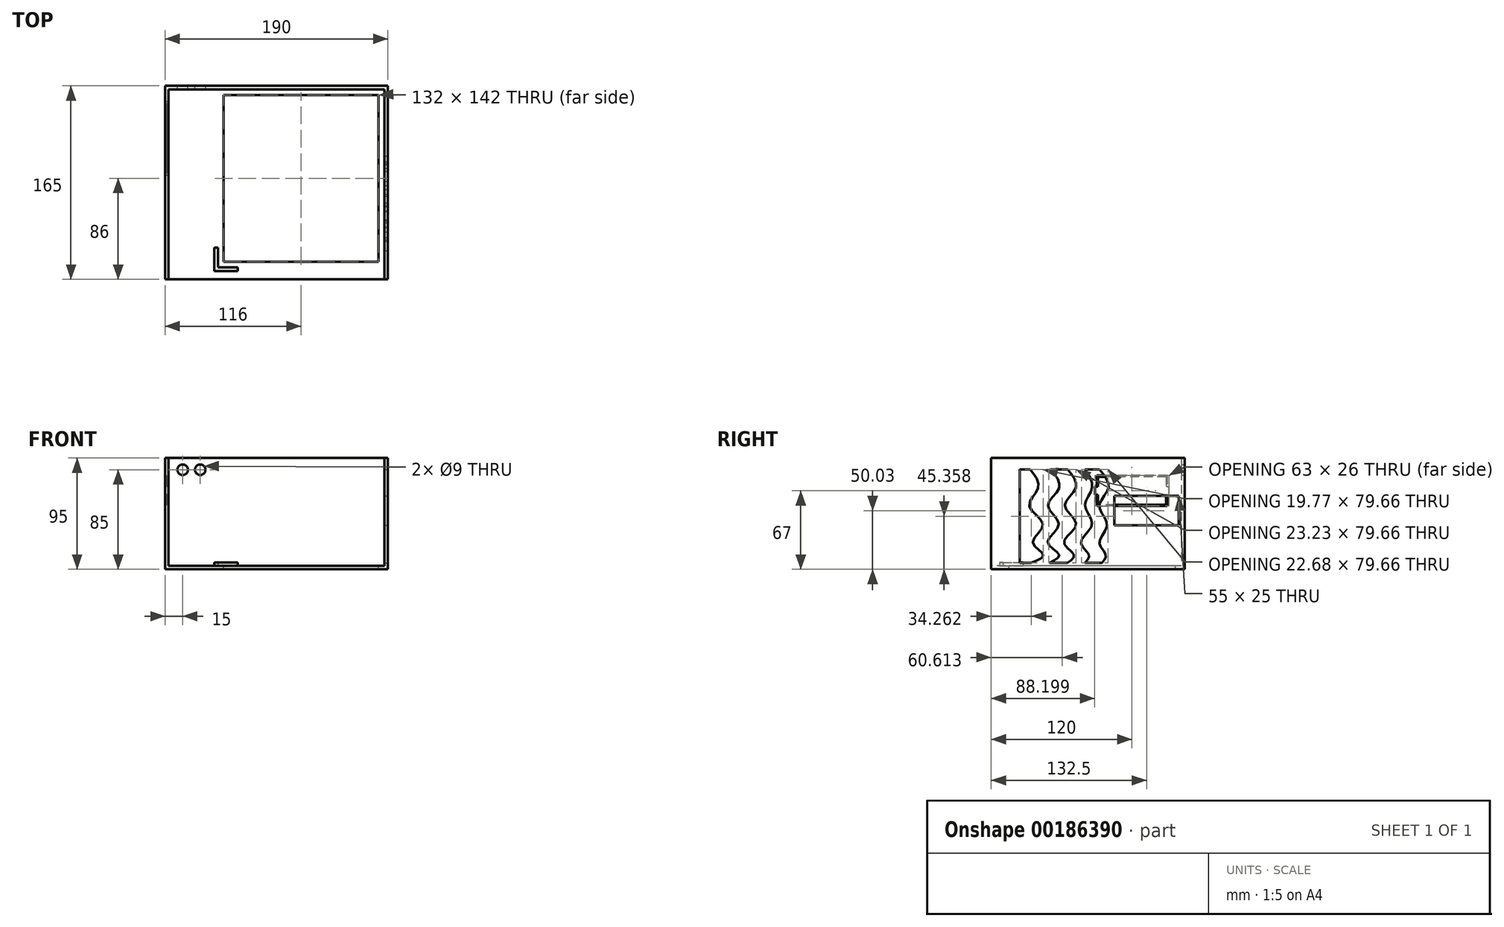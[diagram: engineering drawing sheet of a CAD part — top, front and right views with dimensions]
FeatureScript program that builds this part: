
annotation { "Feature Type Name" : "Feature", "Feature Type Description" : "" }
export const myFeature = defineFeature(function(context is Context, id is Id, definition is map)
    precondition{}
    {
        {
            var Q0;
            Q0=qCreatedBy(makeId("Top.planeOp"),FACE);
            var sketch = newSketch(context, id + "F0", { "sketchPlane" : qUnion([Q0])});
            skLineSegment(sketch, "E0.bottom", {"start": v(-95, 85) * mm, "end": v(95, 85) * mm});
            skLineSegment(sketch, "E0.top", {"start": v(-95, -85) * mm, "end": v(95, -85) * mm});
            skLineSegment(sketch, "E0.left", {"start": v(-95, 85) * mm, "end": v(-95, -85) * mm});
            skLineSegment(sketch, "E0.right", {"start": v(95, 85) * mm, "end": v(95, -85) * mm});
            skPoint(sketch, "E0.middle", {"position": v(0, 0) * mm});
            skSolve(sketch);
        }
        {
            var Q0;
            Q0=makeQuery(id+"F0.imprint","IMPRINT",FACE,{"disambiguationData":[TD([[makeQuery(id+"F0.imprint","IMPRINT",EDGE,{"derivedFrom":sQuery(id+"F0.wireOp",EDGE,"E0.bottom")}),-1.0]])]});
            extrude(context, id + "F1", {"entities" : qUnion([Q0]), "depth" : 95 * mm});
        }
        {
            var Q0;
            Q0=makeQuery(id+"F1.opExtrude","CAP_FACE",FACE,{"disambiguationData":[OSD([sQuery(id+"F0.wireOp",EDGE,"E0.bottom"),sQuery(id+"F0.wireOp",EDGE,"E0.top"),sQuery(id+"F0.wireOp",EDGE,"E0.left"),sQuery(id+"F0.wireOp",EDGE,"E0.right")])],"isStart":false});
            var Q1;
            Q1=makeQuery(id+"F1.opExtrude","SWEPT_FACE",FACE,{"disambiguationData":[OSD([sQuery(id+"F0.wireOp",EDGE,"E0.top")])]});
            shell(context, id + "F2", {"entities" : qUnion([Q0, Q1]), "thickness" : 3 * mm});
        }
        {
            var Q0;
            Q0=makeQuery(id+"F2.opShell","OFFSET_FACE",FACE,{"disambiguationData":[OSD([sQuery(id+"F0.wireOp",EDGE,"E0.bottom"),sQuery(id+"F0.wireOp",EDGE,"E0.top"),sQuery(id+"F0.wireOp",EDGE,"E0.left"),sQuery(id+"F0.wireOp",EDGE,"E0.right")])]});
            var sketch = newSketch(context, id + "F3", { "sketchPlane" : qUnion([Q0])});
            skLineSegment(sketch, "E1.bottom", {"start": v(92, 82) * mm, "end": v(-50, 82) * mm});
            skLineSegment(sketch, "E1.top", {"start": v(92, -70) * mm, "end": v(-50, -70) * mm, "construction": true});
            skLineSegment(sketch, "E1.left", {"start": v(92, 82) * mm, "end": v(92, -70) * mm});
            skLineSegment(sketch, "E1.right", {"start": v(-50, 82) * mm, "end": v(-50, -70) * mm, "construction": true});
            skLineSegment(sketch, "E2.top", {"start": v(-50, -53) * mm, "end": v(-53, -53) * mm});
            skLineSegment(sketch, "E2.left", {"start": v(-50, -70) * mm, "end": v(-50, -53) * mm});
            skLineSegment(sketch, "E2.right", {"start": v(-53, -70) * mm, "end": v(-53, -53) * mm});
            skLineSegment(sketch, "E3.bottom", {"start": v(-50, -70) * mm, "end": v(-33, -70) * mm});
            skLineSegment(sketch, "E3.top", {"start": v(-53, -73) * mm, "end": v(-33, -73) * mm});
            skLineSegment(sketch, "E3.left", {"start": v(-53, -70) * mm, "end": v(-53, -73) * mm});
            skLineSegment(sketch, "E3.right", {"start": v(-33, -70) * mm, "end": v(-33, -73) * mm});
            skSolve(sketch);
        }
        {
            var Q0;
            Q0=makeQuery(id+"F3.imprint","IMPRINT",FACE,{"disambiguationData":[TD([[makeQuery(id+"F3.imprint","IMPRINT",EDGE,{"derivedFrom":sQuery(id+"F3.wireOp",EDGE,"E2.top")}),1.0]])]});
            extrude(context, id + "F4", {"entities" : qUnion([Q0]), "operationType" : NewBodyOperationType.ADD, "depth" : 3 * mm});
        }
        {
            var Q0;
            Q0=makeQuery(id+"F1.opExtrude","SWEPT_FACE",FACE,{"disambiguationData":[OSD([sQuery(id+"F0.wireOp",EDGE,"E0.right")])]});
            var sketch = newSketch(context, id + "F5", { "sketchPlane" : qUnion([Q0])});
            skLineSegment(sketch, "E4.bottom", {"start": v(85, 95) * mm, "end": v(-67, 95) * mm});
            skLineSegment(sketch, "E4.top", {"start": v(85, 3) * mm, "end": v(-67, 3) * mm});
            skLineSegment(sketch, "E4.left", {"start": v(85, 95) * mm, "end": v(85, 3) * mm});
            skLineSegment(sketch, "E4.right", {"start": v(-67, 95) * mm, "end": v(-67, 3) * mm});
            skLineSegment(sketch, "E5.0", {"start": v(-22, 85.19) * mm, "end": v(29.77, 85.19) * mm});
            skLineSegment(sketch, "E6.bottom", {"start": v(-55.62, 85.19) * mm, "end": v(80, 85.19) * mm});
            skLineSegment(sketch, "E6.top", {"start": v(-55.62, 5.53) * mm, "end": v(80, 5.53) * mm});
            skLineSegment(sketch, "E6.left", {"start": v(-55.62, 85.19) * mm, "end": v(-55.62, 5.53) * mm});
            skLineSegment(sketch, "E6.right", {"start": v(80, 85.19) * mm, "end": v(80, 5.53) * mm});
            skLineSegment(sketch, "E7.bottom", {"start": v(80, 37.53) * mm, "end": v(25, 37.53) * mm});
            skLineSegment(sketch, "E7.top", {"start": v(80, 62.53) * mm, "end": v(25, 62.53) * mm});
            skLineSegment(sketch, "E7.left", {"start": v(80, 37.53) * mm, "end": v(80, 62.53) * mm});
            skLineSegment(sketch, "E7.right", {"start": v(25, 37.53) * mm, "end": v(25, 62.53) * mm});
            skPoint(sketch, "E8.orphan", {"position": v(3.89, 5.53) * mm});
            skFitSpline(sketch, "E9", {"points": [v(-46.65, 85.19) * mm, v(-39.93, 69.5) * mm, v(-47.64, 54.07) * mm, v(-35.97, 38.25) * mm, v(-44.47, 23.03) * mm, v(-35.78, 12.55) * mm, v(-46.25, 5.53) * mm], "startDerivative": vector(72.14, -91.85) * mm, "endDerivative": vector(-114.34, -43.57) * mm});
            skFitSpline(sketch, "E10", {"points": [v(-29.25, 85.19) * mm, v(-22.13, 69.5) * mm, v(-31.62, 54.07) * mm, v(-22.33, 38.25) * mm, v(-31.82, 23.03) * mm, v(-22.13, 12.55) * mm, v(-30.24, 5.53) * mm], "startDerivative": vector(76.45, -91.72) * mm, "endDerivative": vector(-99.1, -48.82) * mm});
            skFitSpline(sketch, "E11", {"points": [v(-14.82, 85.19) * mm, v(-7.9, 69.5) * mm, v(-17.19, 54.07) * mm, v(-7.7, 38.25) * mm, v(-17.98, 23.03) * mm, v(-9.48, 12.55) * mm, v(-15.01, 5.53) * mm], "startDerivative": vector(73.81, -90.58) * mm, "endDerivative": vector(-76.43, -53.52) * mm});
            skFitSpline(sketch, "E12", {"points": [v(0, 85.19) * mm, v(5.94, 69.5) * mm, v(0, 54.07) * mm, v(5.94, 38.25) * mm, v(-3.55, 23.03) * mm, v(3.18, 12.55) * mm, v(0, 5.53) * mm], "startDerivative": vector(57.94, -87.76) * mm, "endDerivative": vector(-49.7, -56.04) * mm});
            skPoint(sketch, "E13.2.internal.snap0", {"position": v(12.19, 85.19) * mm});
            skPoint(sketch, "E13.4.internal.snap0", {"position": v(12.19, 85.19) * mm});
            skFitSpline(sketch, "E13", {"points": [v(12.19, 85.19) * mm, v(19.98, 69.5) * mm, v(12.19, 54.07) * mm, v(18.8, 38.25) * mm, v(12.19, 23.03) * mm, v(17.6, 12.55) * mm, v(14.45, 5.53) * mm], "startDerivative": vector(72.92, -85.74) * mm, "endDerivative": vector(-46.67, -55.62) * mm});
            skSolve(sketch);
        }
        {
            var Q0;
            Q0=makeQuery(id+"F1.opExtrude","SWEPT_FACE",FACE,{"disambiguationData":[OSD([sQuery(id+"F0.wireOp",EDGE,"E0.left")])]});
            var sketch = newSketch(context, id + "F6", { "sketchPlane" : qUnion([Q0])});
            skLineSegment(sketch, "E14.bottom", {"start": v(85, 95) * mm, "end": v(80, 95) * mm});
            skLineSegment(sketch, "E14.top", {"start": v(85, 0) * mm, "end": v(80, 0) * mm});
            skLineSegment(sketch, "E14.left", {"start": v(85, 95) * mm, "end": v(85, 0) * mm});
            skLineSegment(sketch, "E14.right", {"start": v(80, 95) * mm, "end": v(80, 0) * mm});
            skSolve(sketch);
        }
        {
            var Q0;
            Q0=makeQuery(id+"F6.imprint","IMPRINT",FACE,{"disambiguationData":[TD([[makeQuery(id+"F6.imprint","IMPRINT",EDGE,{"derivedFrom":sQuery(id+"F6.wireOp",EDGE,"E14.bottom")}),-1.0]])]});
            var Q1;
            Q1=makeQuery(id+"F1.opExtrude","SWEPT_FACE",FACE,{"disambiguationData":[OSD([sQuery(id+"F0.wireOp",EDGE,"E0.right")])]});
            extrude(context, id + "F7", {"entities" : qUnion([Q0]), "operationType" : NewBodyOperationType.REMOVE, "endBound" : BoundingType.UP_TO_SURFACE, "oppositeDirection" : true, "endBoundEntityFace" : qUnion([Q1]), "depth" : 25 * mm});
        }
        {
            var Q0;
            Q0=makeQuery(id+"F5.imprint","IMPRINT",FACE,{"disambiguationData":[TD([[makeQuery(id+"F5.imprint","IMPRINT",EDGE,{"derivedFrom":sQuery(id+"F5.wireOp",EDGE,"E7.bottom")}),-1.0]])]});
            var Q1;
            {var subQ0=sQuery(id+"F5.wireOp",EDGE,"E12");Q1=makeQuery(id+"F5.imprint","IMPRINT",FACE,{"disambiguationData":[TD([[makeQuery(id+"F5.imprint","IMPRINT",EDGE,{"derivedFrom":subQ0}),1.0]])]});}
            var Q2;
            {var subQ3=sQuery(id+"F5.wireOp",EDGE,"E10");Q2=makeQuery(id+"F5.imprint","IMPRINT",FACE,{"disambiguationData":[TD([[makeQuery(id+"F5.imprint","IMPRINT",EDGE,{"derivedFrom":subQ3}),1.0]])]});}
            var Q3;
            {var subQ0=sQuery(id+"F5.wireOp",EDGE,"E6.left");Q3=makeQuery(id+"F5.imprint","IMPRINT",FACE,{"disambiguationData":[TD([[makeQuery(id+"F5.imprint","IMPRINT",EDGE,{"derivedFrom":subQ0}),1.0]])]});}
            extrude(context, id + "F8", {"entities" : qUnion([Q0, Q1, Q2, Q3]), "operationType" : NewBodyOperationType.REMOVE, "oppositeDirection" : true, "depth" : 25 * mm});
        }
        {
            var Q0;
            Q0=makeQuery(id+"F1.opExtrude","SWEPT_FACE",FACE,{"disambiguationData":[OSD([sQuery(id+"F0.wireOp",EDGE,"E0.bottom")])]});
            var sketch = newSketch(context, id + "F9", { "sketchPlane" : qUnion([Q0])});
            skPoint(sketch, "E15", {"position": v(65, 85) * mm});
            skPoint(sketch, "E16", {"position": v(80, 85) * mm});
            skSolve(sketch);
        }
        {
            var Q0;
            Q0=sQuery(id+"F9.wireOp",VERTEX,"E15");
            var Q1;
            Q1=sQuery(id+"F9.wireOp",VERTEX,"E16");
            var Q2;
            Q2=makeQuery(id+"F1.opExtrude","SWEPT_BODY",BODY,{"disambiguationData":[OSD([sQuery(id+"F0.wireOp",EDGE,"E0.bottom"),sQuery(id+"F0.wireOp",EDGE,"E0.top"),sQuery(id+"F0.wireOp",EDGE,"E0.left"),sQuery(id+"F0.wireOp",EDGE,"E0.right")])]});
            hole(context, id + "F10", {"style" : HoleStyle.SIMPLE, "endStyle" : HoleEndStyle.THROUGH, "holeDiameter" : 9 * mm, "locations" : qUnion([Q0, Q1]), "scope" : qUnion([Q2]), "isTappedThrough" : true});
        }
        {
            var Q0;
            Q0=makeQuery(id+"F1.opExtrude","SWEPT_FACE",FACE,{"disambiguationData":[OSD([sQuery(id+"F0.wireOp",EDGE,"E0.left")])]});
            var sketch = newSketch(context, id + "F11", { "sketchPlane" : qUnion([Q0])});
            skLineSegment(sketch, "E17.bottom", {"start": v(-70, 80) * mm, "end": v(-10, 80) * mm});
            skLineSegment(sketch, "E17.top", {"start": v(-70, 54) * mm, "end": v(-10, 54) * mm});
            skLineSegment(sketch, "E17.left", {"start": v(-70, 80) * mm, "end": v(-70, 54) * mm});
            skLineSegment(sketch, "E17.right", {"start": v(-10, 80) * mm, "end": v(-10, 54) * mm});
            skLineSegment(sketch, "E18.bottom", {"start": v(-69, 79) * mm, "end": v(-11, 79) * mm});
            skLineSegment(sketch, "E18.top", {"start": v(-69, 55) * mm, "end": v(-11, 55) * mm});
            skLineSegment(sketch, "E18.left", {"start": v(-69, 79) * mm, "end": v(-69, 55) * mm});
            skLineSegment(sketch, "E18.right", {"start": v(-11, 79) * mm, "end": v(-11, 55) * mm});
            skSolve(sketch);
        }
        {
            var Q0;
            Q0=makeQuery(id+"F11.imprint","IMPRINT",FACE,{"disambiguationData":[TD([[makeQuery(id+"F11.imprint","IMPRINT",EDGE,{"derivedFrom":sQuery(id+"F11.wireOp",EDGE,"E18.bottom")}),-1.0]])]});
            extrude(context, id + "F12", {"entities" : qUnion([Q0]), "operationType" : NewBodyOperationType.REMOVE, "endBound" : BoundingType.UP_TO_NEXT, "oppositeDirection" : true, "depth" : 25 * mm});
        }
        {
            var Q0;
            Q0=makeQuery(id+"F11.imprint","IMPRINT",FACE,{"disambiguationData":[TD([[makeQuery(id+"F11.imprint","IMPRINT",EDGE,{"derivedFrom":sQuery(id+"F11.wireOp",EDGE,"E17.bottom")}),-1.0]])]});
            extrude(context, id + "F13", {"entities" : qUnion([Q0]), "operationType" : NewBodyOperationType.REMOVE, "oppositeDirection" : true, "depth" : 1 * mm});
        }
        {
            var Q0;
            Q0=makeQuery(id+"F2.opShell","OFFSET_FACE",FACE,{"disambiguationData":[OSD([sQuery(id+"F0.wireOp",EDGE,"E0.left")])]});
            var sketch = newSketch(context, id + "F14", { "sketchPlane" : qUnion([Q0])});
            skLineSegment(sketch, "E19.bottom", {"start": v(10, 80) * mm, "end": v(70, 80) * mm});
            skLineSegment(sketch, "E19.top", {"start": v(10, 54) * mm, "end": v(70, 54) * mm});
            skLineSegment(sketch, "E19.left", {"start": v(10, 80) * mm, "end": v(10, 54) * mm});
            skLineSegment(sketch, "E19.right", {"start": v(70, 80) * mm, "end": v(70, 54) * mm});
            skSolve(sketch);
        }
        {
            var Q0;
            Q0=makeQuery(id+"F14.imprint","IMPRINT",FACE,{"disambiguationData":[TD([[makeQuery(id+"F14.imprint","IMPRINT",EDGE,{"derivedFrom":sQuery(id+"F14.wireOp",EDGE,"E19.bottom")}),-1.0]])]});
            extrude(context, id + "F15", {"entities" : qUnion([Q0]), "operationType" : NewBodyOperationType.REMOVE, "oppositeDirection" : true, "depth" : 1 * mm});
        }
        {
            var Q0;
            Q0=makeQuery(id+"F11.imprint","IMPRINT",FACE,{"disambiguationData":[TD([[makeQuery(id+"F11.imprint","IMPRINT",EDGE,{"derivedFrom":sQuery(id+"F11.wireOp",EDGE,"E17.bottom")}),1.0]])]});
            var sketch = newSketch(context, id + "F16", { "sketchPlane" : qUnion([Q0])});
            skLineSegment(sketch, "E20.bottom", {"start": v(-71.5, 70.5) * mm, "end": v(-68.5, 70.5) * mm});
            skLineSegment(sketch, "E20.top", {"start": v(-71.5, 63.5) * mm, "end": v(-68.5, 63.5) * mm});
            skLineSegment(sketch, "E20.left", {"start": v(-71.5, 70.5) * mm, "end": v(-71.5, 63.5) * mm});
            skLineSegment(sketch, "E20.right", {"start": v(-68.5, 70.5) * mm, "end": v(-68.5, 63.5) * mm});
            skPoint(sketch, "E20.middle", {"position": v(-70, 67) * mm});
            skLineSegment(sketch, "E21.bottom", {"start": v(-11.5, 70.5) * mm, "end": v(-8.5, 70.5) * mm});
            skLineSegment(sketch, "E21.top", {"start": v(-11.5, 63.5) * mm, "end": v(-8.5, 63.5) * mm});
            skLineSegment(sketch, "E21.left", {"start": v(-11.5, 70.5) * mm, "end": v(-11.5, 63.5) * mm});
            skLineSegment(sketch, "E21.right", {"start": v(-8.5, 70.5) * mm, "end": v(-8.5, 63.5) * mm});
            skPoint(sketch, "E21.middle", {"position": v(-10, 67) * mm});
            skSolve(sketch);
        }
        {
            var Q0;
            {var subQ0=sQuery(id+"F16.wireOp",EDGE,"E20.left");Q0=makeQuery(id+"F16.imprint","IMPRINT",FACE,{"disambiguationData":[TD([[makeQuery(id+"F16.imprint","IMPRINT",EDGE,{"derivedFrom":subQ0}),1.0]])]});}
            var Q1;
            {var subQ0=sQuery(id+"F16.wireOp",EDGE,"E20.right");Q1=makeQuery(id+"F16.imprint","IMPRINT",FACE,{"disambiguationData":[TD([[makeQuery(id+"F16.imprint","IMPRINT",EDGE,{"derivedFrom":subQ0}),-1.0]])]});}
            var Q2;
            {var subQ0=sQuery(id+"F16.wireOp",EDGE,"E21.left");Q2=makeQuery(id+"F16.imprint","IMPRINT",FACE,{"disambiguationData":[TD([[makeQuery(id+"F16.imprint","IMPRINT",EDGE,{"derivedFrom":subQ0}),1.0]])]});}
            var Q3;
            {var subQ0=sQuery(id+"F16.wireOp",EDGE,"E21.right");Q3=makeQuery(id+"F16.imprint","IMPRINT",FACE,{"disambiguationData":[TD([[makeQuery(id+"F16.imprint","IMPRINT",EDGE,{"derivedFrom":subQ0}),-1.0]])]});}
            extrude(context, id + "F17", {"entities" : qUnion([Q0, Q1, Q2, Q3]), "operationType" : NewBodyOperationType.REMOVE, "oppositeDirection" : true, "depth" : 5 * mm});
        }
        {
            var Q0;
            {var subQ4=sQuery(id+"F3.wireOp",EDGE,"E1.bottom");Q0=makeQuery(id+"F3.imprint","IMPRINT",FACE,{"disambiguationData":[TD([[makeQuery(id+"F3.imprint","IMPRINT",EDGE,{"derivedFrom":subQ4}),-1.0]])]});}
            var sketch = newSketch(context, id + "F18", { "sketchPlane" : qUnion([Q0])});
            skLineSegment(sketch, "E22.bottom", {"start": v(87, 77) * mm, "end": v(-45, 77) * mm});
            skLineSegment(sketch, "E22.top", {"start": v(87, -65) * mm, "end": v(-45, -65) * mm});
            skLineSegment(sketch, "E22.left", {"start": v(87, 77) * mm, "end": v(87, -65) * mm});
            skLineSegment(sketch, "E22.right", {"start": v(-45, 77) * mm, "end": v(-45, -65) * mm});
            skPoint(sketch, "E22.middle", {"position": v(24.55, 0) * mm});
            skSolve(sketch);
        }
        {
            var Q0;
            Q0=makeQuery(id+"F18.imprint","IMPRINT",FACE,{"disambiguationData":[TD([[makeQuery(id+"F18.imprint","IMPRINT",EDGE,{"derivedFrom":sQuery(id+"F18.wireOp",EDGE,"E22.bottom")}),1.0]])]});
            extrude(context, id + "F19", {"entities" : qUnion([Q0]), "operationType" : NewBodyOperationType.REMOVE, "endBound" : BoundingType.THROUGH_ALL, "oppositeDirection" : true, "depth" : 25 * mm});
        }
    });
